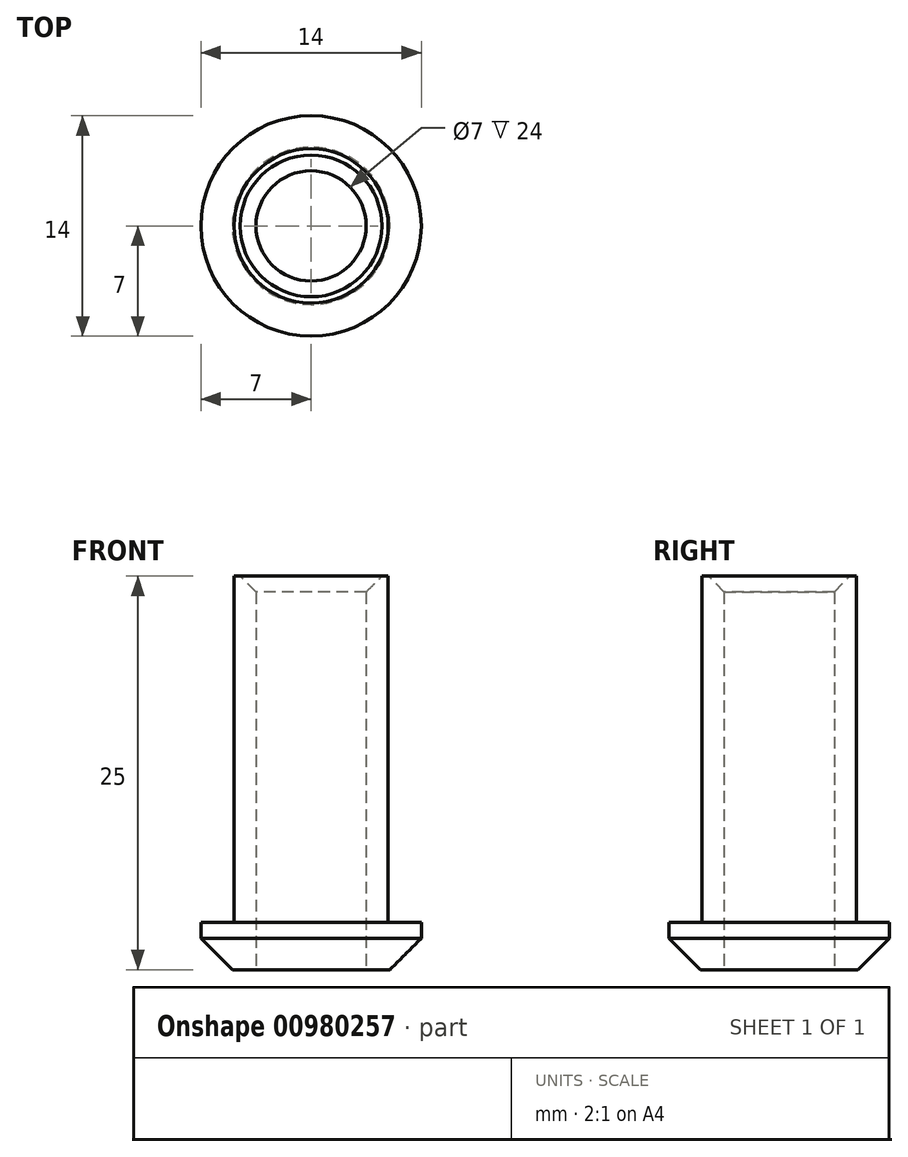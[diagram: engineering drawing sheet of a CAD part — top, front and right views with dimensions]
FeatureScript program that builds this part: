
annotation { "Feature Type Name" : "Feature", "Feature Type Description" : "" }
export const myFeature = defineFeature(function(context is Context, id is Id, definition is map)
    precondition{}
    {
        {
            var Q0;
            Q0=qCreatedBy(makeId("Top.planeOp"),FACE);
            var sketch = newSketch(context, id + "F0", { "sketchPlane" : qUnion([Q0])});
            skCircle(sketch, "E0", {"center": v(0, 0) * mm, "radius": 4.9 * mm});
            skCircle(sketch, "E1", {"center": v(0, 0) * mm, "radius": 3.5 * mm});
            skCircle(sketch, "E2", {"center": v(0, 0) * mm, "radius": 7 * mm});
            skSolve(sketch);
        }
        {
            var Q0;
            Q0=makeQuery(id+"F0.imprint","IMPRINT",FACE,{"disambiguationData":[TD([[makeQuery(id+"F0.imprint","IMPRINT",EDGE,{"derivedFrom":sQuery(id+"F0.wireOp",EDGE,"E0")}),1.0]])]});
            extrude(context, id + "F1", {"entities" : qUnion([Q0]), "depth" : 25 * mm, "offsetDistance" : 25 * mm});
        }
        {
            var Q0;
            Q0=makeQuery(id+"F0.imprint","IMPRINT",FACE,{"disambiguationData":[TD([[makeQuery(id+"F0.imprint","IMPRINT",EDGE,{"derivedFrom":sQuery(id+"F0.wireOp",EDGE,"E0")}),-1.0]])]});
            extrude(context, id + "F2", {"entities" : qUnion([Q0]), "operationType" : NewBodyOperationType.ADD, "depth" : 3 * mm, "offsetDistance" : 25 * mm});
        }
        {
            var Q0;
            Q0=makeQuery(id+"F2.opExtrude","CAP_EDGE",EDGE,{"disambiguationData":[OSD([sQuery(id+"F0.wireOp",EDGE,"E2")])],"isStart":true});
            chamfer(context, id + "F3", {"entities" : qUnion([Q0]), "width" : 2 * mm, "tangentPropagation" : true});
        }
        {
            var Q0;
            Q0=makeQuery(id+"F1.opExtrude","CAP_EDGE",EDGE,{"disambiguationData":[OSD([sQuery(id+"F0.wireOp",EDGE,"E1")])],"isStart":false});
            chamfer(context, id + "F4", {"entities" : qUnion([Q0]), "width" : 1 * mm, "tangentPropagation" : true});
        }
    });
